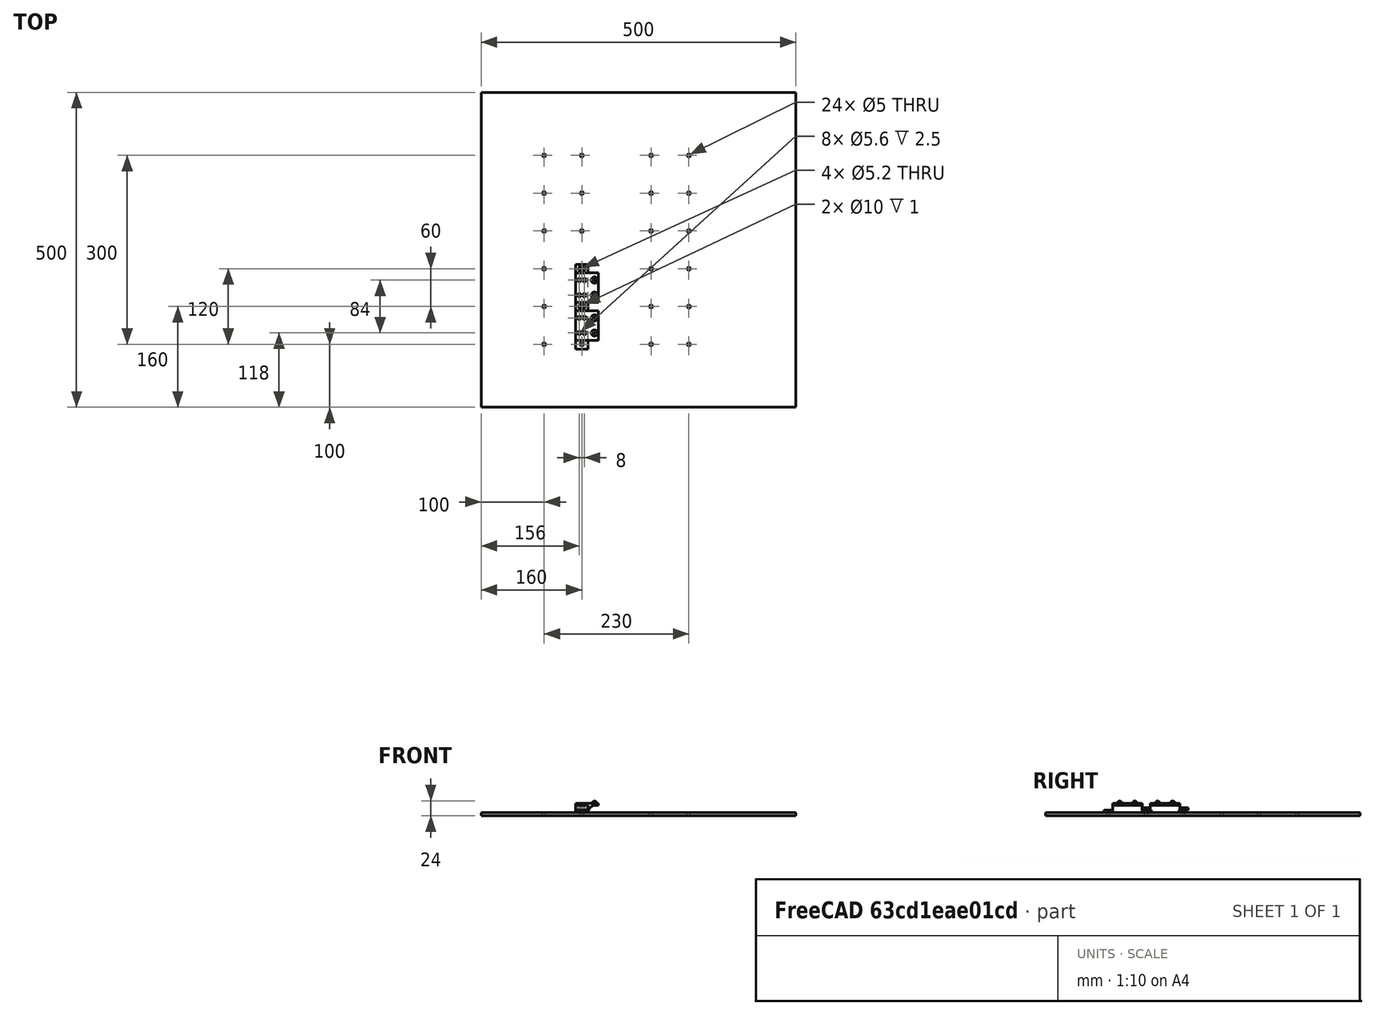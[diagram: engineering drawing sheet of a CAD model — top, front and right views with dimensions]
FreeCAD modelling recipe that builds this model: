
FCSTD DOCUMENT  (FreeCAD 0.19R24366 (Git))
Label: Charmhigh_static_feeders
License: All rights reserved
LicenseURL: http://en.wikipedia.org/wiki/All_rights_reserved
objects: Part::Cylinder×31, Part::MultiFuse×17, Part::Box×13, Part::Cut×7, Part::Feature×3, Part::Refine×1, Part::Fillet×1, Part::Chamfer×1
note: 74 computed .brp shape members not serialized (recipe doc carries the construction recipe); baked Part::Feature solids carry a one-line shape summary decoded from their .brp

FEATURE [Part::Box] Box  label="Cube"
  AttacherType = Attacher::AttachEngine3D
  Height = 5
  Length = 500
  Placement = pos=(0,0,-5) rot=(0,0,1;0rad)
  Width = 500
FEATURE [Part::Cylinder] Cylinder
  Angle = 360
  AttacherType = Attacher::AttachEngine3D
  Height = 5
  Placement = pos=(100,100,-5) rot=(0,0,1;0rad)
  Radius = 2.5
FEATURE [Part::Cylinder] Cylinder001
  Angle = 360
  AttacherType = Attacher::AttachEngine3D
  Height = 5
  Placement = pos=(270,100,-5) rot=(0,0,1;0rad)
  Radius = 2.5
FEATURE [Part::Cylinder] Cylinder002
  Angle = 360
  AttacherType = Attacher::AttachEngine3D
  Height = 5
  Placement = pos=(160,100,-5) rot=(0,0,1;0rad)
  Radius = 2.5
FEATURE [Part::Cylinder] Cylinder003
  Angle = 360
  AttacherType = Attacher::AttachEngine3D
  Height = 5
  Placement = pos=(330,100,-5) rot=(0,0,1;0rad)
  Radius = 2.5
FEATURE [Part::MultiFuse] Fusion
  Shapes = -> [Cylinder,Cylinder001,Cylinder002,Cylinder003]
FEATURE [Part::Cylinder] Cylinder004
  Angle = 360
  AttacherType = Attacher::AttachEngine3D
  Height = 5
  Placement = pos=(160,100,-5) rot=(0,0,1;0rad)
  Radius = 2.5
FEATURE [Part::Cylinder] Cylinder005
  Angle = 360
  AttacherType = Attacher::AttachEngine3D
  Height = 5
  Placement = pos=(270,100,-5) rot=(0,0,1;0rad)
  Radius = 2.5
FEATURE [Part::Cylinder] Cylinder006
  Angle = 360
  AttacherType = Attacher::AttachEngine3D
  Height = 5
  Placement = pos=(330,100,-5) rot=(0,0,1;0rad)
  Radius = 2.5
FEATURE [Part::Cylinder] Cylinder007
  Angle = 360
  AttacherType = Attacher::AttachEngine3D
  Height = 5
  Placement = pos=(100,100,-5) rot=(0,0,1;0rad)
  Radius = 2.5
FEATURE [Part::MultiFuse] Fusion001
  Placement = pos=(0,60,0) rot=(0,0,1;0rad)
  Shapes = -> [Cylinder007,Cylinder005,Cylinder004,Cylinder006]
FEATURE [Part::Cylinder] Cylinder008
  Angle = 360
  AttacherType = Attacher::AttachEngine3D
  Height = 5
  Placement = pos=(160,100,-5) rot=(0,0,1;0rad)
  Radius = 2.5
FEATURE [Part::Cylinder] Cylinder009
  Angle = 360
  AttacherType = Attacher::AttachEngine3D
  Height = 5
  Placement = pos=(270,100,-5) rot=(0,0,1;0rad)
  Radius = 2.5
FEATURE [Part::Cylinder] Cylinder010
  Angle = 360
  AttacherType = Attacher::AttachEngine3D
  Height = 5
  Placement = pos=(330,100,-5) rot=(0,0,1;0rad)
  Radius = 2.5
FEATURE [Part::Cylinder] Cylinder011
  Angle = 360
  AttacherType = Attacher::AttachEngine3D
  Height = 5
  Placement = pos=(100,100,-5) rot=(0,0,1;0rad)
  Radius = 2.5
FEATURE [Part::MultiFuse] Fusion002
  Placement = pos=(0,120,0) rot=(0,0,1;0rad)
  Shapes = -> [Cylinder011,Cylinder009,Cylinder008,Cylinder010]
FEATURE [Part::Cylinder] Cylinder012
  Angle = 360
  AttacherType = Attacher::AttachEngine3D
  Height = 5
  Placement = pos=(160,100,-5) rot=(0,0,1;0rad)
  Radius = 2.5
FEATURE [Part::Cylinder] Cylinder013
  Angle = 360
  AttacherType = Attacher::AttachEngine3D
  Height = 5
  Placement = pos=(270,100,-5) rot=(0,0,1;0rad)
  Radius = 2.5
FEATURE [Part::Cylinder] Cylinder014
  Angle = 360
  AttacherType = Attacher::AttachEngine3D
  Height = 5
  Placement = pos=(330,100,-5) rot=(0,0,1;0rad)
  Radius = 2.5
FEATURE [Part::Cylinder] Cylinder015
  Angle = 360
  AttacherType = Attacher::AttachEngine3D
  Height = 5
  Placement = pos=(100,100,-5) rot=(0,0,1;0rad)
  Radius = 2.5
FEATURE [Part::MultiFuse] Fusion003
  Placement = pos=(0,180,0) rot=(0,0,1;0rad)
  Shapes = -> [Cylinder015,Cylinder013,Cylinder012,Cylinder014]
FEATURE [Part::Cylinder] Cylinder016
  Angle = 360
  AttacherType = Attacher::AttachEngine3D
  Height = 5
  Placement = pos=(160,100,-5) rot=(0,0,1;0rad)
  Radius = 2.5
FEATURE [Part::Cylinder] Cylinder017
  Angle = 360
  AttacherType = Attacher::AttachEngine3D
  Height = 5
  Placement = pos=(270,100,-5) rot=(0,0,1;0rad)
  Radius = 2.5
FEATURE [Part::Cylinder] Cylinder018
  Angle = 360
  AttacherType = Attacher::AttachEngine3D
  Height = 5
  Placement = pos=(330,100,-5) rot=(0,0,1;0rad)
  Radius = 2.5
FEATURE [Part::Cylinder] Cylinder019
  Angle = 360
  AttacherType = Attacher::AttachEngine3D
  Height = 5
  Placement = pos=(100,100,-5) rot=(0,0,1;0rad)
  Radius = 2.5
FEATURE [Part::MultiFuse] Fusion004
  Placement = pos=(0,240,0) rot=(0,0,1;0rad)
  Shapes = -> [Cylinder019,Cylinder017,Cylinder016,Cylinder018]
FEATURE [Part::Cylinder] Cylinder020
  Angle = 360
  AttacherType = Attacher::AttachEngine3D
  Height = 5
  Placement = pos=(160,100,-5) rot=(0,0,1;0rad)
  Radius = 2.5
FEATURE [Part::Cylinder] Cylinder021
  Angle = 360
  AttacherType = Attacher::AttachEngine3D
  Height = 5
  Placement = pos=(270,100,-5) rot=(0,0,1;0rad)
  Radius = 2.5
FEATURE [Part::Cylinder] Cylinder022
  Angle = 360
  AttacherType = Attacher::AttachEngine3D
  Height = 5
  Placement = pos=(330,100,-5) rot=(0,0,1;0rad)
  Radius = 2.5
FEATURE [Part::Cylinder] Cylinder023
  Angle = 360
  AttacherType = Attacher::AttachEngine3D
  Height = 5
  Placement = pos=(100,100,-5) rot=(0,0,1;0rad)
  Radius = 2.5
FEATURE [Part::MultiFuse] Fusion005
  Placement = pos=(0,300,0) rot=(0,0,1;0rad)
  Shapes = -> [Cylinder023,Cylinder021,Cylinder020,Cylinder022]
FEATURE [Part::MultiFuse] Fusion006
  Shapes = -> [Fusion,Fusion001,Fusion002,Fusion003,Fusion004,Fusion005]
FEATURE [Part::Cut] Cut
  Base = -> Box
  Tool = -> Fusion006
FEATURE [Part::Feature] Cut007007  label="BOTTOM001"
  Placement = pos=(140,107.5,12) rot=(0,0,1;0rad)
  shape: bbox 150 x 23 x 7 mm, 18 faces (baked)
FEATURE [Part::Box] Box001  label="Cube001"
  AttacherType = Attacher::AttachEngine3D
  Height = 12
  Length = 20
  Placement = pos=(150,92.5,0) rot=(0,0,1;0rad)
  Width = 75
FEATURE [Part::Box] Box002  label="Cube002"
  AttacherType = Attacher::AttachEngine3D
  Height = 8
  Length = 20
  Placement = pos=(150,92.5,4) rot=(0,0,1;0rad)
  Width = 15
FEATURE [Part::Cylinder] Cylinder024
  Angle = 360
  AttacherType = Attacher::AttachEngine3D
  Height = 4
  Placement = pos=(160,100,0) rot=(0,0,1;0rad)
  Radius = 2.6
FEATURE [Part::MultiFuse] Fusion007
  Shapes = -> [Cylinder024,Box002]
FEATURE [Part::Cut] Cut007008
  Base = -> Box001
  Tool = -> Fusion007
FEATURE [Part::Box] Box003  label="DELETOR_01"
  AttacherType = Attacher::AttachEngine3D
  Height = 15
  Length = 120
  Placement = pos=(186,107.5,8) rot=(0,0,1;0rad)
  Width = 23
FEATURE [Part::Box] Box004  label="DELETOR_002"
  AttacherType = Attacher::AttachEngine3D
  Height = 10
  Length = 120
  Placement = pos=(30,107.5,8) rot=(0,0,1;0rad)
  Width = 23
FEATURE [Part::MultiFuse] Fusion008
  Shapes = -> [Box003,Box004]
FEATURE [Part::Cut] Cut007009
  Base = -> Cut007007
  Placement = pos=(0,-1,0) rot=(0,0,1;0rad)
  Tool = -> Fusion008
FEATURE [Part::Box] Box006  label="Cube004"
  AttacherType = Attacher::AttachEngine3D
  Height = 8
  Length = 20
  Placement = pos=(150,92.5,4) rot=(0,0,1;0rad)
  Width = 15
FEATURE [Part::Cylinder] Cylinder025
  Angle = 360
  AttacherType = Attacher::AttachEngine3D
  Height = 4
  Placement = pos=(160,100,0) rot=(0,0,1;0rad)
  Radius = 2.6
FEATURE [Part::MultiFuse] Fusion009
  Placement = pos=(0,60,0) rot=(0,0,1;0rad)
  Shapes = -> [Cylinder025,Box006]
FEATURE [Part::Cut] Cut007010
  Base = -> Cut007008
  Tool = -> Fusion009
FEATURE [Part::Feature] Cut007009001
  Placement = pos=(0,23,0) rot=(0,0,1;0rad)
  shape: bbox 36 x 23 x 7 mm, 12 faces (baked)
FEATURE [Part::MultiFuse] Fusion010
  Shapes = -> [Cut007009,Cut007010,Cut007009001]
FEATURE [Part::Box] Box007  label="Cube005"
  AttacherType = Attacher::AttachEngine3D
  Height = 12
  Length = 16
  Placement = pos=(170,106.5,0) rot=(0,0,1;0rad)
  Width = 47
FEATURE [Part::Cylinder] Cylinder026
  Angle = 360
  AttacherType = Attacher::AttachEngine3D
  Height = 47
  Placement = pos=(182,153.5,0) rot=(1,0,0;1.5708rad)
  Radius = 12
FEATURE [Part::Box] Box008  label="Cube006"
  AttacherType = Attacher::AttachEngine3D
  Height = 12
  Length = 4
  Placement = pos=(182,106.5,0) rot=(0,0,1;0rad)
  Width = 47
FEATURE [Part::MultiFuse] Fusion011
  Shapes = -> [Box008,Cylinder026]
FEATURE [Part::Cut] Cut007009002  label="big fillet"
  Base = -> Box007
  Tool = -> Fusion011
FEATURE [Part::MultiFuse] Fusion012
  Shapes = -> [Fusion010,Cut007009002]
FEATURE [Part::Box] Box009  label="Cube007"
  AttacherType = Attacher::AttachEngine3D
  Height = 3
  Length = 36
  Placement = pos=(150,129.5,12) rot=(0,0,1;0rad)
  Width = 1
FEATURE [Part::MultiFuse] Fusion013
  Shapes = -> [Fusion012,Box009]
FEATURE [Part::Refine] Fusion013001
  Source = -> Fusion013
FEATURE [Part::Fillet] Fillet  label="BASE_A"
  Base = -> Fusion013001
  Edges = 2 edges r=0.9: [Edge3,Edge32]
FEATURE [Part::Feature] Fillet001
  Placement = pos=(0,60,0) rot=(0,0,1;0rad)
  shape: bbox 36 x 75 x 19 mm, 36 faces (baked)
FEATURE [Part::Box] Box010  label="Cube008"
  AttacherType = Attacher::AttachEngine3D
  Height = 4
  Length = 22
  Placement = pos=(150,152.5,0) rot=(0,0,1;0rad)
  Width = 15.5
FEATURE [Part::Box] Box011  label="Cube009"
  AttacherType = Attacher::AttachEngine3D
  Height = 4
  Length = 22
  Placement = pos=(150,212,0) rot=(0,0,1;0rad)
  Width = 15.5
FEATURE [Part::Box] Box012  label="Cube010"
  AttacherType = Attacher::AttachEngine3D
  Height = 3.8
  Length = 20
  Placement = pos=(150,153,4.2) rot=(0,0,1;0rad)
  Width = 14.5
FEATURE [Part::Box] Box013  label="Cube011"
  AttacherType = Attacher::AttachEngine3D
  Height = 3.8
  Length = 20
  Placement = pos=(150,212.5,4.2) rot=(0,0,1;0rad)
  Width = 14.5
FEATURE [Part::Cylinder] Cylinder027
  Angle = 360
  AttacherType = Attacher::AttachEngine3D
  Height = 4
  Placement = pos=(160,160,4) rot=(0,0,1;0rad)
  Radius = 2.6
FEATURE [Part::Cylinder] Cylinder028
  Angle = 360
  AttacherType = Attacher::AttachEngine3D
  Height = 4
  Placement = pos=(160,220,4) rot=(0,0,1;0rad)
  Radius = 2.6
FEATURE [Part::MultiFuse] Fusion013002
  Shapes = -> [Box011,Box010]
FEATURE [Part::Cut] Cut007009003
  Base = -> Fillet001
  Tool = -> Fusion013002
FEATURE [Part::Cylinder] Cylinder029
  Angle = 360
  AttacherType = Attacher::AttachEngine3D
  Height = 1
  Placement = pos=(160,160,7) rot=(0,0,1;0rad)
  Radius = 5
FEATURE [Part::Cylinder] Cylinder030
  Angle = 360
  AttacherType = Attacher::AttachEngine3D
  Height = 1
  Placement = pos=(160,220,7) rot=(0,0,1;0rad)
  Radius = 5
FEATURE [Part::MultiFuse] Fusion013003
  Shapes = -> [Cylinder030,Cylinder029,Cylinder028,Cylinder027]
FEATURE [Part::MultiFuse] Fusion013004
  Shapes = -> [Cut007009003,Box013,Box012]
FEATURE [Part::Cut] Cut007009004
  Base = -> Fusion013004
  Tool = -> Fusion013003
FEATURE [Part::Chamfer] Chamfer  label="BASE_B"
  Base = -> Cut007009004
  Edges = 2 edges r=2: [Edge28,Edge109]
